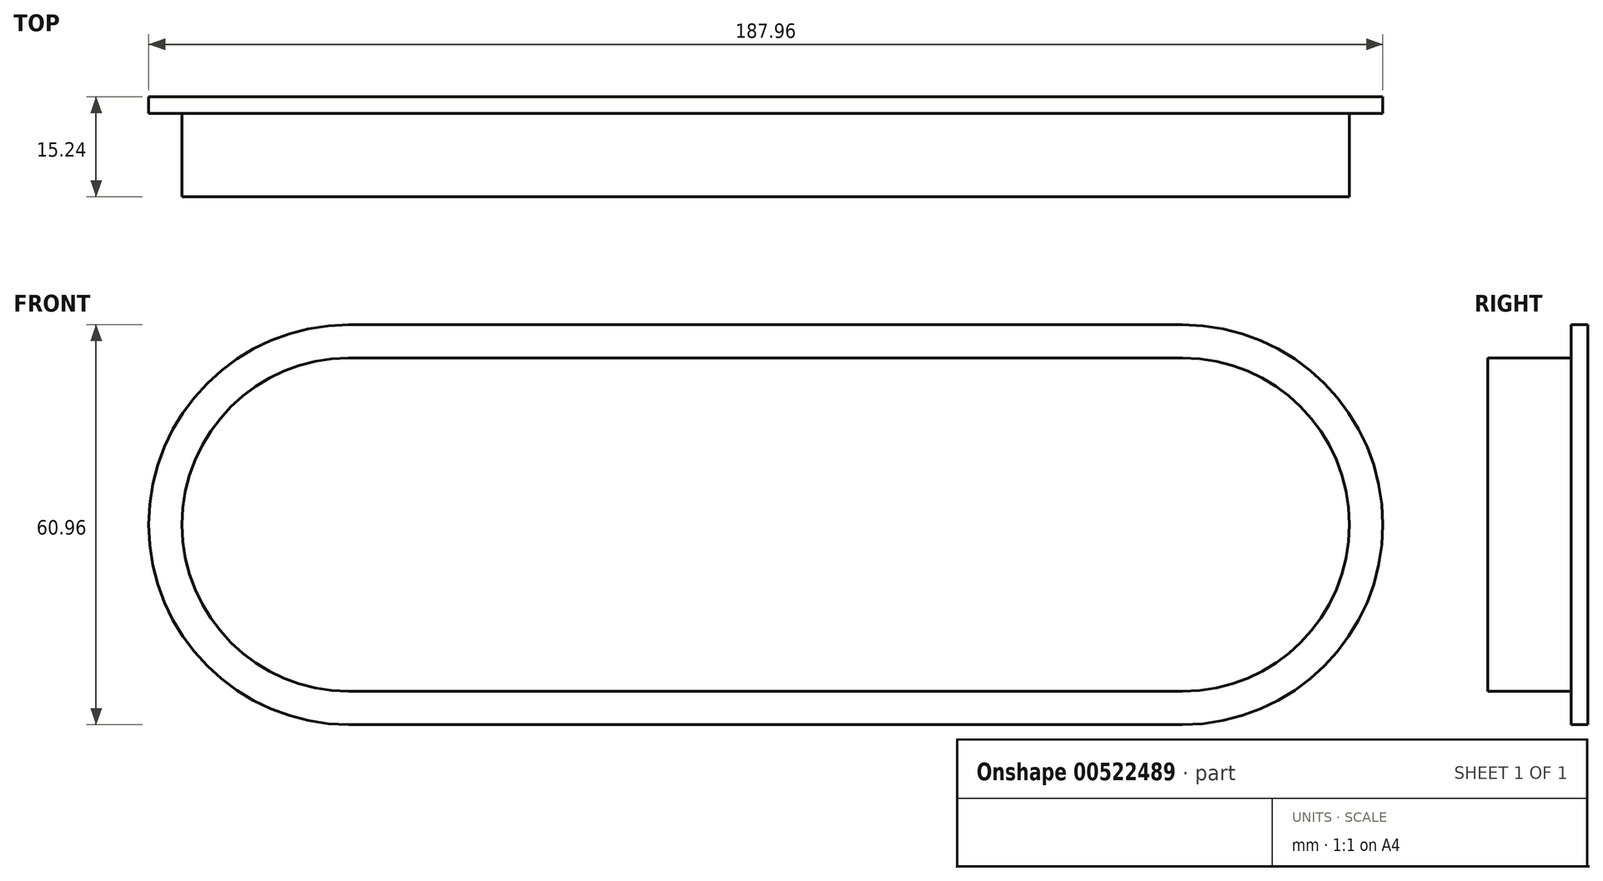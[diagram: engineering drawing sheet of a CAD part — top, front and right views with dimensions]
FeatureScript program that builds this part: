
annotation { "Feature Type Name" : "Feature", "Feature Type Description" : "" }
export const myFeature = defineFeature(function(context is Context, id is Id, definition is map)
    precondition{}
    {
        {
            var Q0;
            Q0=qCreatedBy(makeId("Front.planeOp"),FACE);
            var sketch = newSketch(context, id + "F0", { "sketchPlane" : qUnion([Q0])});
            skLineSegment(sketch, "E0", {"start": v(-63.5, 0) * mm, "end": v(63.5, 0) * mm});
            skArc(sketch, "E1.0.startCap", {"start": v(-63.5, -25.4) * mm, "mid": v(-88.9, 0) * mm, "end": v(-63.5, 25.4) * mm});
            skArc(sketch, "E1.0.endCap", {"start": v(63.5, 25.4) * mm, "mid": v(88.9, 0) * mm, "end": v(63.5, -25.4) * mm});
            skLineSegment(sketch, "E1.0.left", {"start": v(-63.5, 25.4) * mm, "end": v(63.5, 25.4) * mm});
            skLineSegment(sketch, "E1.0.right", {"start": v(-63.5, -25.4) * mm, "end": v(63.5, -25.4) * mm});
            skLineSegment(sketch, "E2.0", {"start": v(-63.5, 30.48) * mm, "end": v(63.5, 30.48) * mm});
            skArc(sketch, "E2.1", {"start": v(-63.5, -30.48) * mm, "mid": v(-93.98, 0) * mm, "end": v(-63.5, 30.48) * mm});
            skLineSegment(sketch, "E2.2", {"start": v(-63.5, -30.48) * mm, "end": v(63.5, -30.48) * mm});
            skArc(sketch, "E2.3", {"start": v(63.5, 30.48) * mm, "mid": v(93.98, 0) * mm, "end": v(63.5, -30.48) * mm});
            skSolve(sketch);
        }
        {
            var Q0;
            Q0=makeQuery(id+"F0.imprint","IMPRINT",FACE,{"disambiguationData":[TD([[makeQuery(id+"F0.imprint","IMPRINT",EDGE,{"derivedFrom":sQuery(id+"F0.wireOp",EDGE,"E1.0.startCap")}),1.0]])]});
            extrude(context, id + "F1", {"entities" : qUnion([Q0]), "depth" : 12.7 * mm, "offsetDistance" : 25.4 * mm});
        }
        {
            var Q0;
            Q0=makeQuery(id+"F0.imprint","IMPRINT",FACE,{"disambiguationData":[TD([[makeQuery(id+"F0.imprint","IMPRINT",EDGE,{"derivedFrom":sQuery(id+"F0.wireOp",EDGE,"E1.0.startCap")}),-1.0]])]});
            var Q1;
            Q1=makeQuery(id+"F0.imprint","IMPRINT",FACE,{"disambiguationData":[TD([[makeQuery(id+"F0.imprint","IMPRINT",EDGE,{"derivedFrom":sQuery(id+"F0.wireOp",EDGE,"E1.0.startCap")}),1.0]])]});
            extrude(context, id + "F2", {"entities" : qUnion([Q0, Q1]), "operationType" : NewBodyOperationType.ADD, "oppositeDirection" : true, "depth" : 2.54 * mm, "offsetDistance" : 25.4 * mm});
        }
    });
